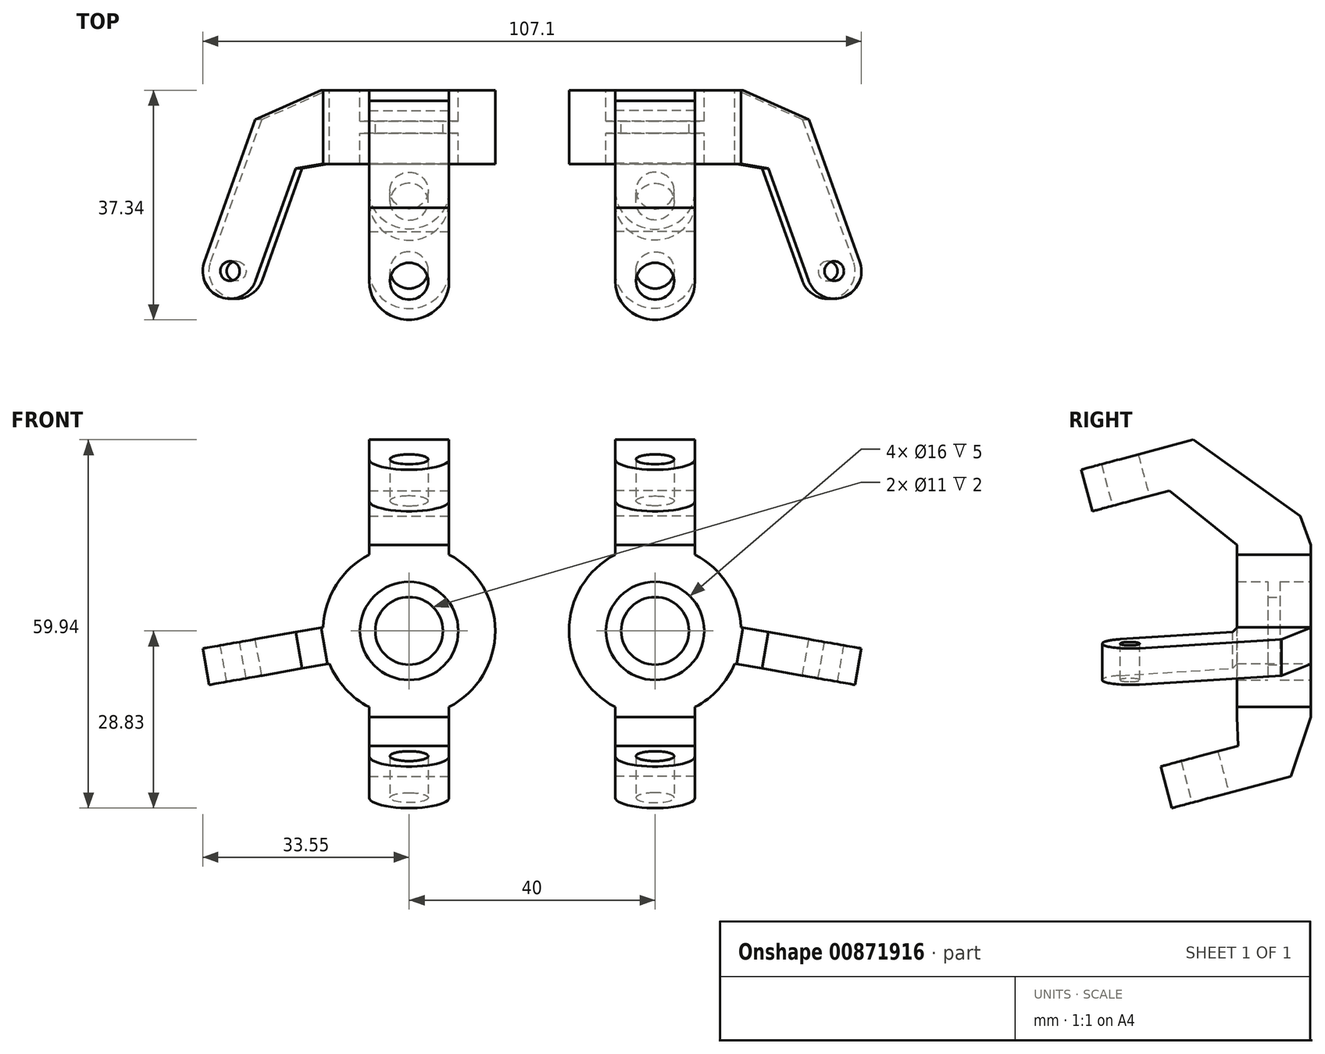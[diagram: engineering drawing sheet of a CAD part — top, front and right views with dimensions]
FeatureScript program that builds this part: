
annotation { "Feature Type Name" : "Feature", "Feature Type Description" : "" }
export const myFeature = defineFeature(function(context is Context, id is Id, definition is map)
    precondition{}
    {
        {
            var Q0;
            Q0=qCreatedBy(makeId("Front.planeOp"),FACE);
            var sketch = newSketch(context, id + "F0", { "sketchPlane" : qUnion([Q0])});
            skCircle(sketch, "E0", {"center": v(0, 0) * mm, "radius": 14 * mm});
            skSolve(sketch);
        }
        {
            var Q0;
            Q0=qSketchRegion(id+"F0",true);
            extrude(context, id + "F1", {"entities" : qUnion([Q0]), "depth" : 12 * mm, "offsetDistance" : 25 * mm});
        }
        {
            var Q0;
            Q0=qCreatedBy(makeId("Right.planeOp"),FACE);
            var sketch = newSketch(context, id + "F2", { "sketchPlane" : qUnion([Q0])});
            skLineSegment(sketch, "E1", {"start": v(0, 0) * mm, "end": v(0, -88) * mm, "construction": true});
            skLineSegment(sketch, "E2", {"start": v(0, -88) * mm, "end": v(-29.25, 21.15) * mm, "construction": true});
            skLineSegment(sketch, "E3", {"start": v(-24.4, -22.07) * mm, "end": v(-18.12, -20.39) * mm, "construction": true});
            skLineSegment(sketch, "E4", {"start": v(-35.53, 19.47) * mm, "end": v(-29.25, 21.15) * mm, "construction": true});
            skLineSegment(sketch, "E5", {"start": v(-35.53, 19.47) * mm, "end": v(-37.34, 26.23) * mm});
            skLineSegment(sketch, "E6", {"start": v(-37.34, 26.23) * mm, "end": v(-19.1, 31.11) * mm});
            skLineSegment(sketch, "E7", {"start": v(-19.1, 31.11) * mm, "end": v(0, 14) * mm, "construction": true});
            skLineSegment(sketch, "E8", {"start": v(-12, 14) * mm, "end": v(-22.97, 22.83) * mm});
            skLineSegment(sketch, "E9", {"start": v(-22.97, 22.83) * mm, "end": v(-35.53, 19.47) * mm});
            skLineSegment(sketch, "E10", {"start": v(-24.4, -22.07) * mm, "end": v(-22.58, -28.83) * mm});
            skLineSegment(sketch, "E11", {"start": v(-22.58, -28.83) * mm, "end": v(-3.27, -23.65) * mm});
            skLineSegment(sketch, "E12", {"start": v(-3.27, -23.65) * mm, "end": v(0, -14) * mm});
            skLineSegment(sketch, "E13", {"start": v(-12, -14) * mm, "end": v(-11.84, -18.7) * mm});
            skLineSegment(sketch, "E14", {"start": v(-11.84, -18.7) * mm, "end": v(-24.4, -22.07) * mm});
            skLineSegment(sketch, "E15", {"start": v(0, -14) * mm, "end": v(-12, -14) * mm, "construction": true});
            skLineSegment(sketch, "E16", {"start": v(0, 14) * mm, "end": v(-12, 14) * mm, "construction": true});
            skLineSegment(sketch, "E17", {"start": v(-11.84, -18.7) * mm, "end": v(-3.27, -23.65) * mm, "construction": true});
            skLineSegment(sketch, "E18", {"start": v(-7.55, -21.18) * mm, "end": v(-23.49, -25.45) * mm, "construction": true});
            skLineSegment(sketch, "E19", {"start": v(-19.1, 31.11) * mm, "end": v(-22.97, 22.83) * mm, "construction": true});
            skLineSegment(sketch, "E20", {"start": v(-21.04, 26.97) * mm, "end": v(-36.43, 22.85) * mm, "construction": true});
            skLineSegment(sketch, "E21", {"start": v(-21.04, 26.97) * mm, "end": v(-6, 14) * mm, "construction": true});
            skLineSegment(sketch, "E22", {"start": v(-6, 14) * mm, "end": v(-6, -14) * mm, "construction": true});
            skLineSegment(sketch, "E23", {"start": v(-6, -14) * mm, "end": v(-7.55, -21.18) * mm, "construction": true});
            skLineSegment(sketch, "E24.0", {"start": v(0, -14) * mm, "end": v(0, 14) * mm});
            skLineSegment(sketch, "E25.0", {"start": v(-12, -14) * mm, "end": v(-12, 14) * mm});
            skLineSegment(sketch, "E26", {"start": v(-19.1, 31.11) * mm, "end": v(-1.71, 18.7) * mm});
            skLineSegment(sketch, "E27", {"start": v(-1.71, 18.7) * mm, "end": v(0, 14) * mm});
            skSolve(sketch);
        }
        {
            var Q0;
            Q0=qSketchRegion(id+"F2",true);
            extrude(context, id + "F3", {"entities" : qUnion([Q0]), "operationType" : NewBodyOperationType.ADD, "oppositeDirection" : true, "depth" : 13 * mm, "offsetDistance" : 25 * mm, "symmetric" : true});
        }
        {
            var Q0;
            Q0=makeQuery(id+"F3.opExtrude","CAP_EDGE",EDGE,{"disambiguationData":[OSD([sQuery(id+"F2.wireOp",EDGE,"E5")])],"isStart":false});
            var Q1;
            Q1=makeQuery(id+"F3.opExtrude","CAP_EDGE",EDGE,{"disambiguationData":[OSD([sQuery(id+"F2.wireOp",EDGE,"E5")])],"isStart":true});
            var Q2;
            Q2=makeQuery(id+"F3.opExtrude","CAP_EDGE",EDGE,{"disambiguationData":[OSD([sQuery(id+"F2.wireOp",EDGE,"E10")])],"isStart":false});
            var Q3;
            Q3=makeQuery(id+"F3.opExtrude","CAP_EDGE",EDGE,{"disambiguationData":[OSD([sQuery(id+"F2.wireOp",EDGE,"E10")])],"isStart":true});
            fillet(context, id + "F4", {"entities" : qUnion([Q0, Q1, Q2, Q3]), "radius" : 6.5 * mm, "tangentPropagation" : true, "allowEdgeOverflow" : false});
        }
        {
            var Q0;
            Q0=makeQuery(id+"F3.opExtrude","SWEPT_FACE",FACE,{"disambiguationData":[OSD([sQuery(id+"F2.wireOp",EDGE,"E11")])]});
            var sketch = newSketch(context, id + "F5", { "sketchPlane" : qUnion([Q0])});
            skCircle(sketch, "E28", {"center": v(0, 22.78) * mm, "radius": 3.1 * mm});
            skSolve(sketch);
        }
        {
            var Q0;
            Q0=qSketchRegion(id+"F5",true);
            extrude(context, id + "F6", {"entities" : qUnion([Q0]), "operationType" : NewBodyOperationType.REMOVE, "endBound" : BoundingType.THROUGH_ALL, "oppositeDirection" : true, "depth" : 25 * mm, "offsetDistance" : 25 * mm});
        }
        {
            var Q0;
            Q0=qCreatedBy(makeId("Top.planeOp"),FACE);
            var sketch = newSketch(context, id + "F7", { "sketchPlane" : qUnion([Q0])});
            skLineSegment(sketch, "E29", {"start": v(0, 0) * mm, "end": v(0, -59.2) * mm, "construction": true});
            skSolve(sketch);
        }
        {
            var Q0;
            Q0=sQuery(id+"F7.wireOp",EDGE,"E29");
            var Q1;
            Q1=qCreatedBy(makeId("Top.planeOp"),FACE);
            cPlane(context, id + "F8", {"entities" : qUnion([Q0, Q1]), "cplaneType" : CPlaneType.LINE_ANGLE, "offset" : 15 * mm, "angle" : 10 * degree, "width" : 150 * mm, "height" : 150 * mm});
        }
        {
            var Q0;
            Q0=qCreatedBy(id+"F8.planeOp",FACE);
            var sketch = newSketch(context, id + "F9", { "sketchPlane" : qUnion([Q0])});
            skArc(sketch, "E30", {"start": v(-24.81, 30.95) * mm, "mid": v(-30.58, 33.64) * mm, "end": v(-33.27, 27.87) * mm});
            skCircle(sketch, "E31", {"center": v(-29.04, 29.4) * mm, "radius": 1.6 * mm});
            skLineSegment(sketch, "E32", {"start": v(-29.04, 29.4) * mm, "end": v(-21.52, 8.74) * mm, "construction": true});
            skLineSegment(sketch, "E33", {"start": v(-24.81, 30.95) * mm, "end": v(-33.27, 27.87) * mm, "construction": true});
            skLineSegment(sketch, "E34", {"start": v(-24.81, 30.95) * mm, "end": v(-18.18, 12.72) * mm});
            skLineSegment(sketch, "E35", {"start": v(-14, 6) * mm, "end": v(-21.52, 8.74) * mm, "construction": true});
            skLineSegment(sketch, "E36", {"start": v(-14, 12) * mm, "end": v(-18.18, 12.72) * mm});
            skLineSegment(sketch, "E37", {"start": v(-33.27, 27.87) * mm, "end": v(-24.86, 4.76) * mm});
            skLineSegment(sketch, "E38", {"start": v(-24.86, 4.76) * mm, "end": v(-14, 0) * mm});
            skLineSegment(sketch, "E39", {"start": v(-18.18, 12.72) * mm, "end": v(-24.86, 4.76) * mm, "construction": true});
            skLineSegment(sketch, "E40", {"start": v(-3.97, 0) * mm, "end": v(-3.97, 12) * mm});
            skLineSegment(sketch, "E41", {"start": v(-3.97, 0) * mm, "end": v(-14, 0) * mm});
            skLineSegment(sketch, "E42", {"start": v(-3.97, 12) * mm, "end": v(-14, 12) * mm});
            skLineSegment(sketch, "E43", {"start": v(-14, 0) * mm, "end": v(-14, 12) * mm, "construction": true});
            skSolve(sketch);
        }
        {
            var Q0;
            Q0=qSketchRegion(id+"F9",true);
            extrude(context, id + "F10", {"entities" : qUnion([Q0]), "operationType" : NewBodyOperationType.ADD, "depth" : 6 * mm, "offsetDistance" : 25 * mm, "symmetric" : true});
        }
        {
            var Q0;
            Q0=qCreatedBy(makeId("Right.planeOp"),FACE);
            var sketch = newSketch(context, id + "F11", { "sketchPlane" : qUnion([Q0])});
            skLineSegment(sketch, "E44", {"start": v(0, 8) * mm, "end": v(-5, 8) * mm});
            skLineSegment(sketch, "E45", {"start": v(-5, 8) * mm, "end": v(-5, 5.5) * mm});
            skLineSegment(sketch, "E46", {"start": v(-5, 5.5) * mm, "end": v(-7, 5.5) * mm});
            skLineSegment(sketch, "E47", {"start": v(-7, 5.5) * mm, "end": v(-7, 8) * mm});
            skLineSegment(sketch, "E48", {"start": v(-7, 8) * mm, "end": v(-12, 8) * mm});
            skLineSegment(sketch, "E49", {"start": v(0, 0) * mm, "end": v(-12, 0) * mm});
            skLineSegment(sketch, "E50", {"start": v(0, 0) * mm, "end": v(0, 8) * mm});
            skLineSegment(sketch, "E51.0", {"start": v(-12, 0) * mm, "end": v(-12, 8) * mm});
            skPoint(sketch, "E52.orphan", {"position": v(-12, 14) * mm});
            skPoint(sketch, "E53.orphan", {"position": v(-12, -14) * mm});
            skLineSegment(sketch, "E54", {"start": v(0, 0) * mm, "end": v(5.22, 0) * mm, "construction": true});
            skSolve(sketch);
        }
        {
            var Q0;
            Q0=qSketchRegion(id+"F11",true);
            var Q1;
            Q1=sQuery(id+"F11.wireOp",EDGE,"E54");
            revolve(context, id + "F12", {"operationType" : NewBodyOperationType.REMOVE, "surfaceOperationType" : NewSurfaceOperationType.NEW, "entities" : qUnion([Q0]), "axis" : qUnion([Q1]), "revolveType" : RevolveType.FULL, "oppositeDirection" : true});
        }
        {
            var Q0;
            Q0=qCreatedBy(makeId("Right.planeOp"),FACE);
            cPlane(context, id + "F13", {"entities" : qUnion([Q0]), "cplaneType" : CPlaneType.OFFSET, "offset" : 20 * mm, "width" : 150 * mm, "height" : 150 * mm});
        }
        {
            var Q0;
            Q0=makeQuery(id+"F1.opExtrude","SWEPT_BODY",BODY,{"disambiguationData":[OSD([sQuery(id+"F0.wireOp",EDGE,"E0")])]});
            var Q1;
            Q1=qCreatedBy(id+"F13.planeOp",FACE);
            mirror(context, id + "F14", {"entities" : qUnion([Q0]), "mirrorPlane" : qUnion([Q1])});
        }
    });
